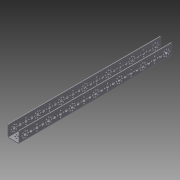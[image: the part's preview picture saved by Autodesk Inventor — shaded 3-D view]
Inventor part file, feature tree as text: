
AUTODESK INVENTOR PART (.ipt)
format: ipt  version: 2013 (Build 170138000, 138)  size: 535,040 bytes
history: native  units: mm
features: hole x28, other x5, sheet_metal_op x4, sketch x3, extrude x1, fillet x1
ambient origin geometry x8: Origin, YZ Plane, XZ Plane, XY Plane, X Axis, Y Axis, Z Axis, Center Point
bodies: Solid1 (feature_tree)
feature tree (42):
  other  "Blocks"
  sheet_metal_op  "Face1"
  sheet_metal_op  "Flange1"
  extrude  "Extrusion1"  Depth=416.0mm
  fillet  "Fillet1"  Radius=16.0mm
  sketch  "Sketch1"  dims[d0=32.0mm d1=416.0mm d3=16.0mm d4=3.7mm]
  hole  "Hole Pattern 4"  [1 undecoded]
  hole  "Hole Pattern 8"  [1 undecoded]
  other  "Plate1"
  sketch  "Sketch2"  dims[d6=16.0mm d8=16.0mm]
  other  "Plate2"
  sheet_metal_op  "Bend1"
  sheet_metal_op  "Corner1"
  sketch  "Sketch3"  dims[d9=16.0mm d10=8.0mm d13=3.7mm d14=8.0mm d15=80.0mm d17=360.0deg d20=16.0mm d21=16.0mm d22=16.0mm d23=16.0mm d25=16.0mm d26=16.0mm d27=2.0mm d28=2.0mm d29=1.0mm d30=4.0mm d31=2.0mm d32=32.0mm d33=90.0deg d34=2.0mm d35=8.0mm d36=2.0mm d37=2.0mm d38=16.0mm d39=16.0mm d40=16.0mm d41=16.0mm d42=16.0mm d43=16.0mm d45=16.0mm d46=10.0mm d47=0.0mm d48=2.0mm]
  other  "416 mm hole pattern"
  hole  "Hole Pattern 4:1"  [1 undecoded]
  hole  "Hole Pattern 8:1"  [1 undecoded]
  hole  "Hole Pattern 8:2"  [1 undecoded]
  hole  "Hole Pattern 4:2"  [1 undecoded]
  hole  "Hole Pattern 8:3"  [1 undecoded]
  hole  "Hole Pattern 4:3"  [1 undecoded]
  hole  "Hole Pattern 8:4"  [1 undecoded]
  hole  "Hole Pattern 4:4"  [1 undecoded]
  hole  "Hole Pattern 8:5"  [1 undecoded]
  hole  "Hole Pattern 8:6"  [1 undecoded]
  hole  "Hole Pattern 4:5"  [1 undecoded]
  hole  "Hole Pattern 8:7"  [1 undecoded]
  hole  "Hole Pattern 4:6"  [1 undecoded]
  other  "416 mm hole pattern:1"
  hole  "Hole Pattern 4:13"  [1 undecoded]
  hole  "Hole Pattern 8:15"  [1 undecoded]
  hole  "Hole Pattern 8:16"  [1 undecoded]
  hole  "Hole Pattern 4:14"  [1 undecoded]
  hole  "Hole Pattern 8:17"  [1 undecoded]
  hole  "Hole Pattern 4:15"  [1 undecoded]
  hole  "Hole Pattern 8:18"  [1 undecoded]
  hole  "Hole Pattern 4:16"  [1 undecoded]
  hole  "Hole Pattern 8:19"  [1 undecoded]
  hole  "Hole Pattern 8:20"  [1 undecoded]
  hole  "Hole Pattern 4:17"  [1 undecoded]
  hole  "Hole Pattern 8:21"  [1 undecoded]
  hole  "Hole Pattern 4:18"  [1 undecoded]
note: 28 required parameter values undecoded (feature->parameter linkage not recoverable at this tier; creation-order binding heuristic only, values carry confidence <= 0.55)
